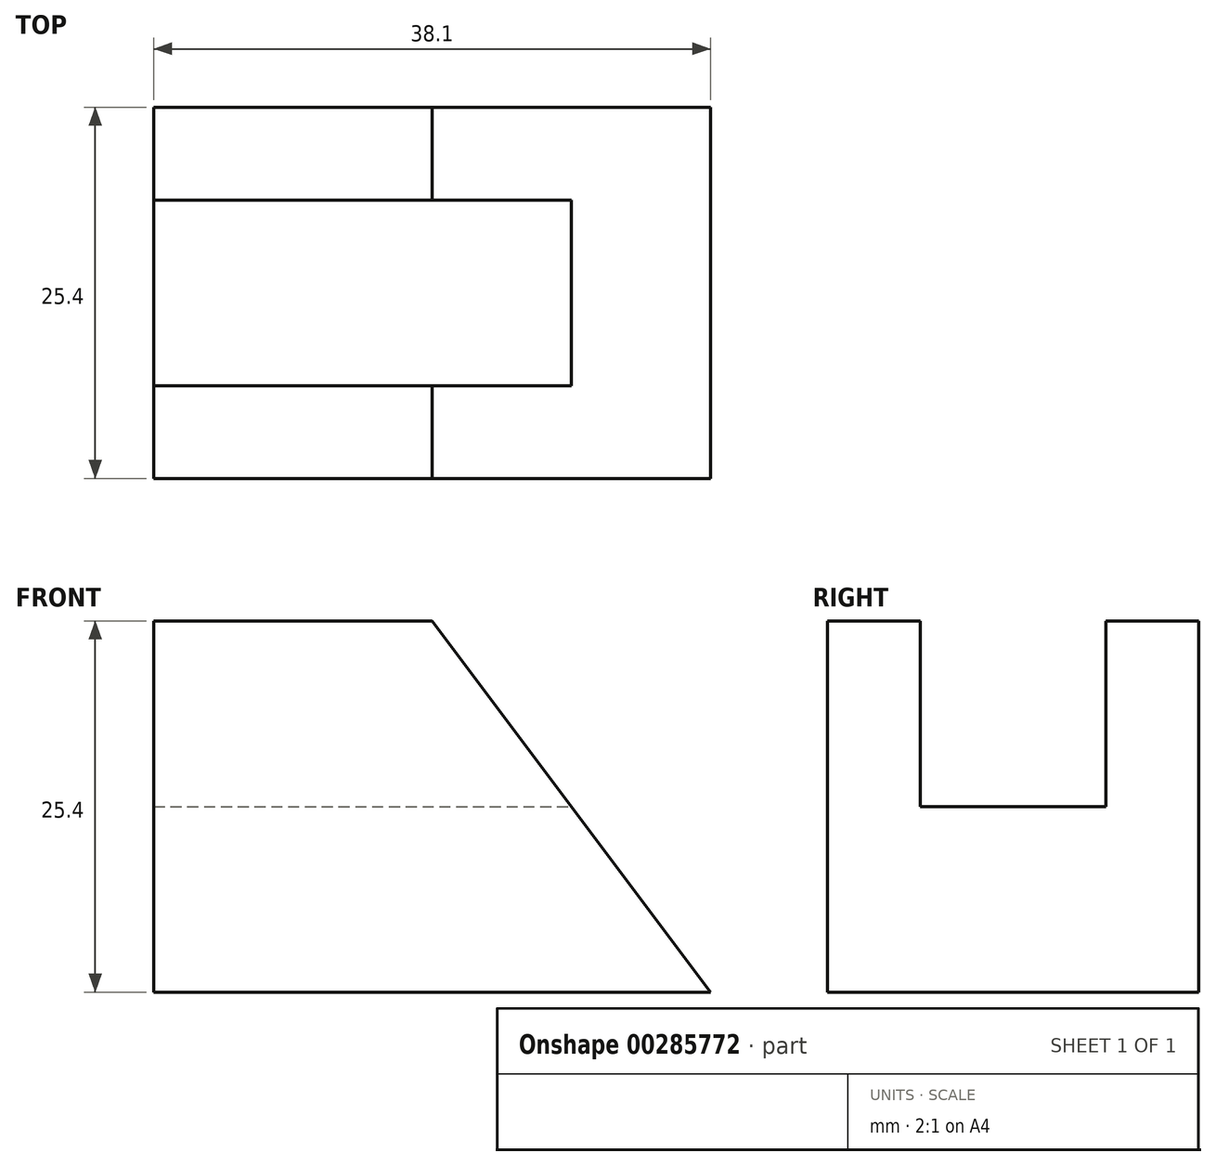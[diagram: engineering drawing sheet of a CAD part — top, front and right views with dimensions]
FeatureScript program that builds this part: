
annotation { "Feature Type Name" : "Feature", "Feature Type Description" : "" }
export const myFeature = defineFeature(function(context is Context, id is Id, definition is map)
    precondition{}
    {
        {
            var Q0;
            Q0=qCreatedBy(makeId("Front.planeOp"),FACE);
            var sketch = newSketch(context, id + "F0", { "sketchPlane" : qUnion([Q0])});
            skLineSegment(sketch, "E0", {"start": v(0, 0) * mm, "end": v(38.1, 0) * mm});
            skLineSegment(sketch, "E1", {"start": v(38.1, 0) * mm, "end": v(19.05, 25.4) * mm});
            skLineSegment(sketch, "E2", {"start": v(19.05, 25.4) * mm, "end": v(0, 25.4) * mm});
            skLineSegment(sketch, "E3", {"start": v(0, 25.4) * mm, "end": v(0, 0) * mm});
            skSolve(sketch);
        }
        {
            var Q0;
            Q0=makeQuery(id+"F0.imprint","IMPRINT",FACE,{"disambiguationData":[TD([[makeQuery(id+"F0.imprint","IMPRINT",EDGE,{"derivedFrom":sQuery(id+"F0.wireOp",EDGE,"E0")}),1.0]])]});
            extrude(context, id + "F1", {"entities" : qUnion([Q0]), "endBound" : BoundingType.SYMMETRIC, "depth" : 25.4 * mm});
        }
        {
            var Q0;
            Q0=makeQuery(id+"F1.opExtrude","SWEPT_FACE",FACE,{"disambiguationData":[OSD([sQuery(id+"F0.wireOp",EDGE,"E2")])]});
            var sketch = newSketch(context, id + "F2", { "sketchPlane" : qUnion([Q0])});
            skLineSegment(sketch, "E4", {"start": v(0, 6.35) * mm, "end": v(31.75, 6.35) * mm});
            skLineSegment(sketch, "E5", {"start": v(31.75, 6.35) * mm, "end": v(31.75, -6.35) * mm});
            skLineSegment(sketch, "E6", {"start": v(31.75, -6.35) * mm, "end": v(0, -6.35) * mm});
            skSolve(sketch);
        }
        {
            var Q0;
            Q0 = qSketchRegion(id + "F2", true);
            var Q1;
            {var subQ0=sQuery(id+"F2.wireOp",EDGE,"E4");var subQ1=sQuery(id+"F0.wireOp",EDGE,"E2");var subQ2=makeQuery(id+"F1.opExtrude","SWEPT_EDGE",EDGE,{"disambiguationData":[OSD([subQ1,sQuery(id+"F0.wireOp",EDGE,"E3")])]});var subQ3=makeQuery(id+"F2.imprint","INTERSECT",VERTEX,{"derivedFrom":[subQ2,subQ0]});Q1=makeQuery(id+"F2.imprint","IMPRINT",FACE,{"disambiguationData":[TD([[makeQuery(id+"F2.imprint","IMPRINT",EDGE,{"disambiguationData":[TD([[subQ3,-1.0]])],"derivedFrom":subQ0}),-1.0]])]});}
            var Q2;
            {var subQ0=sQuery(id+"F2.wireOp",EDGE,"E5");Q2=makeQuery(id+"F2.imprint","IMPRINT",FACE,{"disambiguationData":[TD([[makeQuery(id+"F2.imprint","IMPRINT",EDGE,{"derivedFrom":subQ0}),-1.0]])]});}
            extrude(context, id + "F3", {"entities" : qUnion([Q0, Q1, Q2]), "operationType" : NewBodyOperationType.REMOVE, "oppositeDirection" : true, "depth" : 12.7 * mm});
        }
    });
